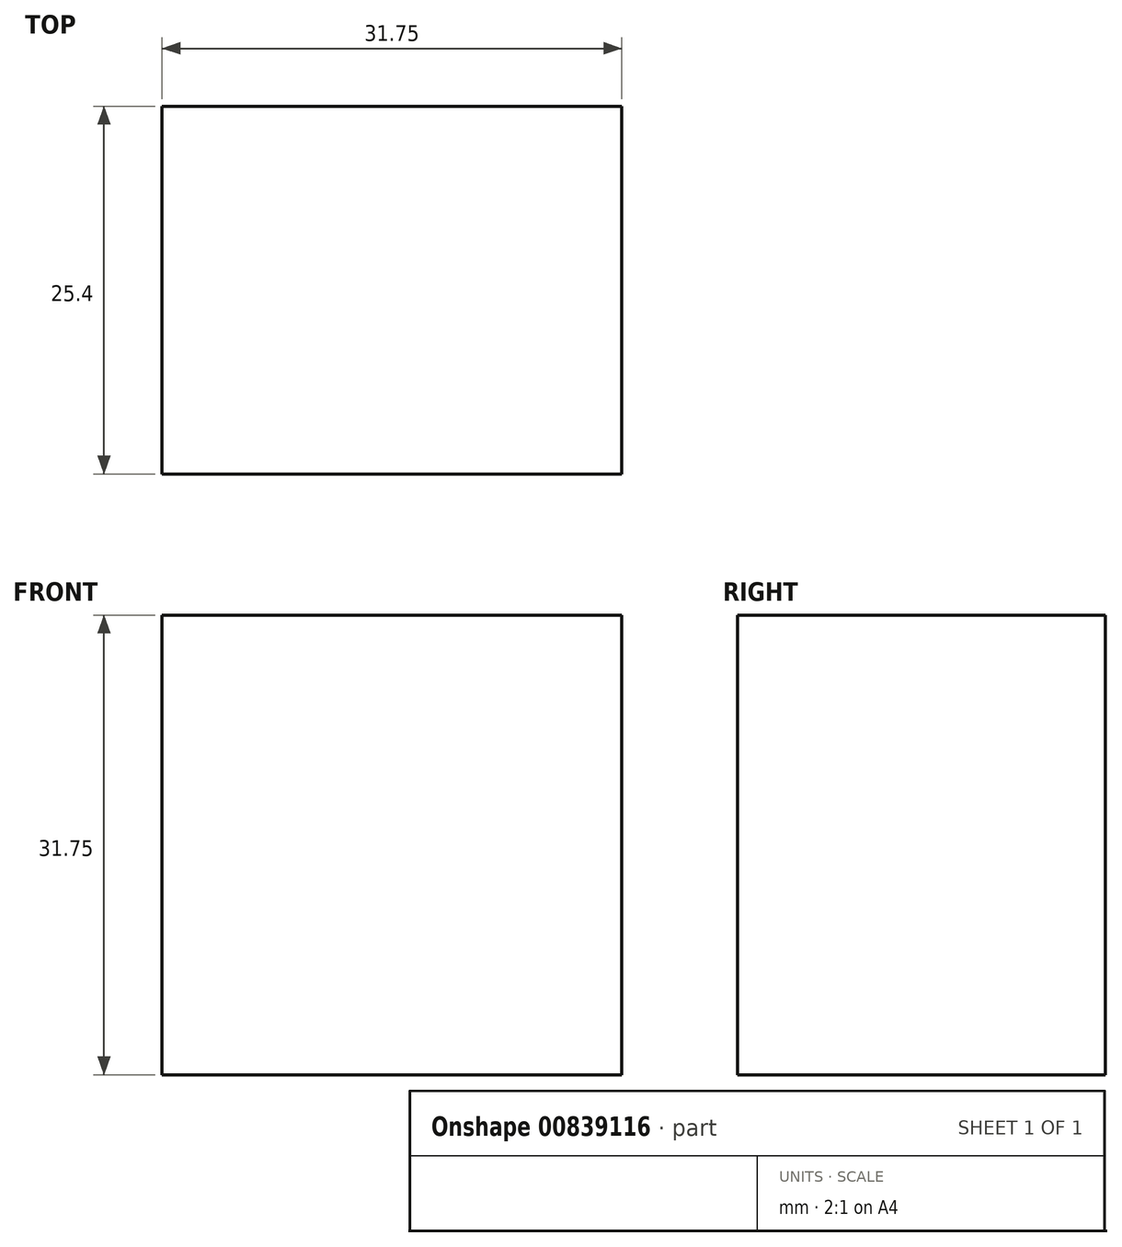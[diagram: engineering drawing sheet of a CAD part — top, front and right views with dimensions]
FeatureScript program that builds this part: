
annotation { "Feature Type Name" : "Feature", "Feature Type Description" : "" }
export const myFeature = defineFeature(function(context is Context, id is Id, definition is map)
    precondition{}
    {
        {
            var Q0;
            Q0=qCreatedBy(makeId("Front.planeOp"),FACE);
            var sketch = newSketch(context, id + "F0", { "sketchPlane" : qUnion([Q0])});
            skLineSegment(sketch, "E0.bottom", {"start": v(0, 0) * mm, "end": v(31.75, 0) * mm});
            skLineSegment(sketch, "E0.top", {"start": v(0, 31.75) * mm, "end": v(31.75, 31.75) * mm});
            skLineSegment(sketch, "E0.left", {"start": v(0, 0) * mm, "end": v(0, 31.75) * mm});
            skLineSegment(sketch, "E0.right", {"start": v(31.75, 0) * mm, "end": v(31.75, 31.75) * mm});
            skSolve(sketch);
        }
        {
            var Q0;
            Q0=makeQuery(id+"F0.imprint","IMPRINT",FACE,{"disambiguationData":[TD([[makeQuery(id+"F0.imprint","IMPRINT",EDGE,{"derivedFrom":sQuery(id+"F0.wireOp",EDGE,"E0.bottom")}),1.0]])]});
            extrude(context, id + "F1", {"entities" : qUnion([Q0]), "depth" : 25.4 * mm, "offsetDistance" : 25.4 * mm});
        }
    });
